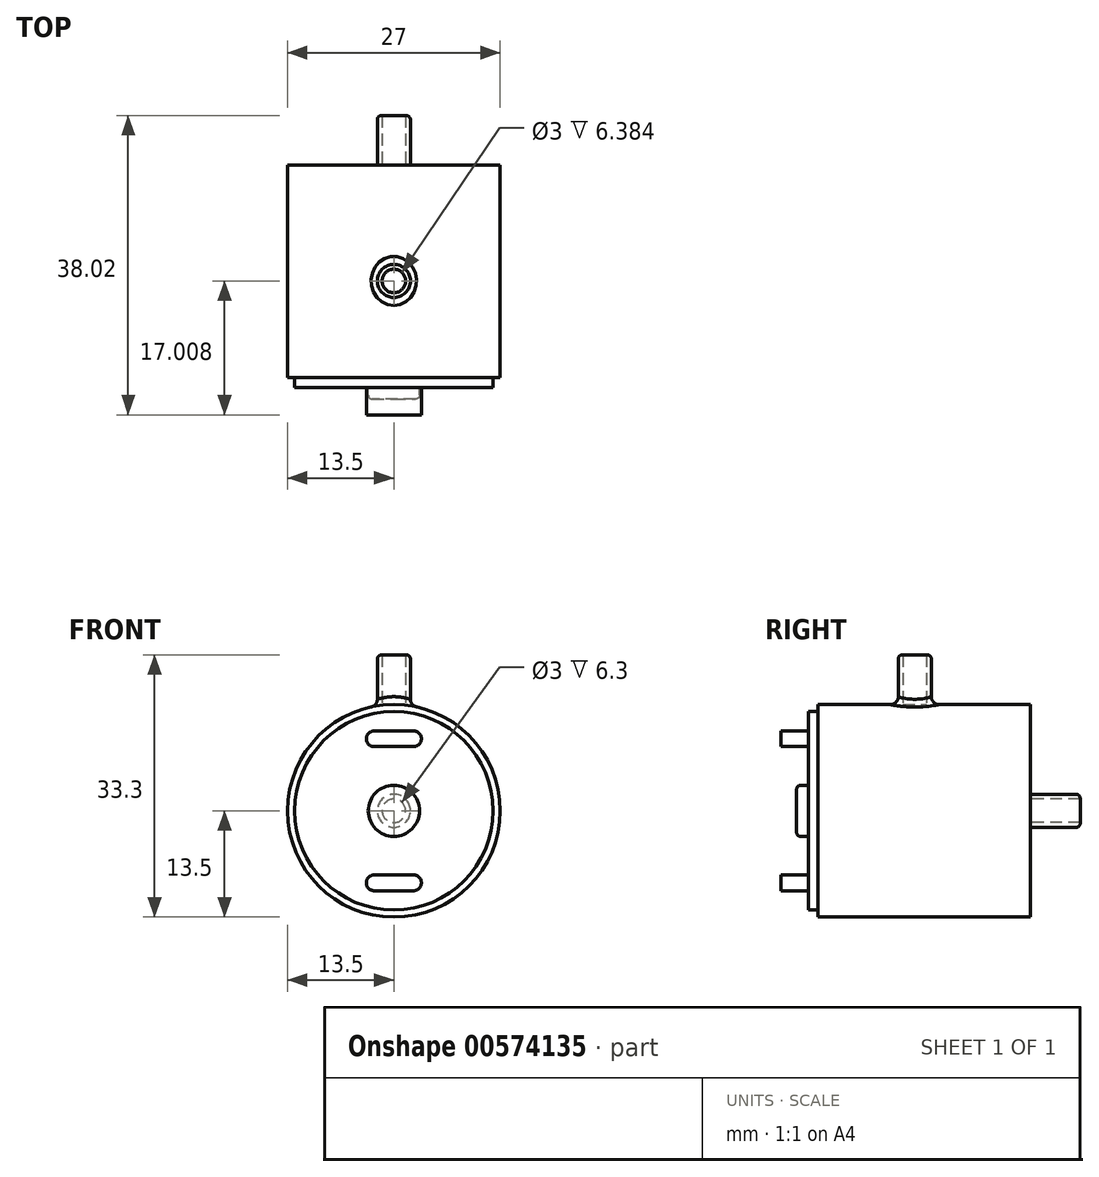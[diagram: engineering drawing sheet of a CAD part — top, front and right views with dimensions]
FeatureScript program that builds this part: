
annotation { "Feature Type Name" : "Feature", "Feature Type Description" : "" }
export const myFeature = defineFeature(function(context is Context, id is Id, definition is map)
    precondition{}
    {
        {
            var Q0;
            Q0=qCreatedBy(makeId("Front.planeOp"),FACE);
            var sketch = newSketch(context, id + "F0", { "sketchPlane" : qUnion([Q0])});
            skCircle(sketch, "E0", {"center": v(0, 0) * mm, "radius": 13.5 * mm});
            skSolve(sketch);
        }
        {
            var Q0;
            Q0 = qSketchRegion(id + "F0", true);
            extrude(context, id + "F1", {"entities" : qUnion([Q0]), "depth" : 27 * mm, "offsetDistance" : 25.4 * mm});
        }
        {
            var Q0;
            Q0=makeQuery(id+"F1.opExtrude","CAP_FACE",FACE,{"disambiguationData":[OSD([sQuery(id+"F0.wireOp",EDGE,"E0")])],"isStart":false});
            var sketch = newSketch(context, id + "F2", { "sketchPlane" : qUnion([Q0])});
            skCircle(sketch, "E1", {"center": v(0, 0) * mm, "radius": 12.6 * mm});
            skSolve(sketch);
        }
        {
            var Q0;
            Q0 = qSketchRegion(id + "F2", true);
            extrude(context, id + "F3", {"entities" : qUnion([Q0]), "operationType" : NewBodyOperationType.ADD, "depth" : ((58 - 27) / 25.4) * mm, "offsetDistance" : 25.4 * mm});
        }
        {
            var Q0;
            Q0=makeQuery(id+"F1.opExtrude","CAP_FACE",FACE,{"disambiguationData":[OSD([sQuery(id+"F0.wireOp",EDGE,"E0")])],"isStart":true});
            var sketch = newSketch(context, id + "F4", { "sketchPlane" : qUnion([Q0])});
            skCircle(sketch, "E2", {"center": v(0, 0) * mm, "radius": 2.1 * mm});
            skCircle(sketch, "E3", {"center": v(0, 0) * mm, "radius": 1.5 * mm});
            skSolve(sketch);
        }
        {
            var Q0;
            Q0 = qSketchRegion(id + "F4", true);
            extrude(context, id + "F5", {"entities" : qUnion([Q0]), "operationType" : NewBodyOperationType.ADD, "depth" : 6.3 * mm, "offsetDistance" : 25.4 * mm});
        }
        {
            var Q0;
            Q0=qCreatedBy(makeId("Top.planeOp"),FACE);
            var sketch = newSketch(context, id + "F6", { "sketchPlane" : qUnion([Q0])});
            skCircle(sketch, "E4", {"center": v(0, -14.71) * mm, "radius": 2.1 * mm});
            skCircle(sketch, "E5", {"center": v(0, -14.71) * mm, "radius": 1.5 * mm});
            skSolve(sketch);
        }
        {
            var Q0;
            Q0 = qSketchRegion(id + "F6", true);
            extrude(context, id + "F7", {"entities" : qUnion([Q0]), "operationType" : NewBodyOperationType.ADD, "depth" : 19.8 * mm, "offsetDistance" : 25.4 * mm});
        }
        {
            var Q0;
            Q0=makeQuery(id+"F5.opExtrude","CAP_EDGE",EDGE,{"disambiguationData":[OSD([sQuery(id+"F4.wireOp",EDGE,"E2")])],"isStart":true});
            var Q1;
            Q1=makeQuery(id+"F7.boolean.opBoolean","INTERSECT",EDGE,{"derivedFrom":[makeQuery(id+"F1.opExtrude","SWEPT_FACE",FACE,{"disambiguationData":[OSD([sQuery(id+"F0.wireOp",EDGE,"E0")])]}),makeQuery(id+"F7.opExtrude","SWEPT_FACE",FACE,{"disambiguationData":[OSD([sQuery(id+"F6.wireOp",EDGE,"E4")])]})]});
            fillet(context, id + "F8", {"entities" : qUnion([Q0, Q1]), "radius" : 1 * mm, "tangentPropagation" : true, "allowEdgeOverflow" : false});
        }
        {
            var Q0;
            Q0=makeQuery(id+"F3.opExtrude","CAP_FACE",FACE,{"disambiguationData":[OSD([sQuery(id+"F2.wireOp",EDGE,"E1")])],"isStart":false});
            var sketch = newSketch(context, id + "F9", { "sketchPlane" : qUnion([Q0])});
            skLineSegment(sketch, "E6", {"start": v(-2.5, 10.15) * mm, "end": v(2.5, 10.15) * mm});
            skLineSegment(sketch, "E7", {"start": v(2.5, 8.15) * mm, "end": v(-2.5, 8.15) * mm});
            skArc(sketch, "E8", {"start": v(-2.5, 10.15) * mm, "mid": v(-3.5, 9.15) * mm, "end": v(-2.5, 8.15) * mm});
            skArc(sketch, "E9", {"start": v(2.5, 8.15) * mm, "mid": v(3.5, 9.15) * mm, "end": v(2.5, 10.15) * mm});
            skPoint(sketch, "E10", {"position": v(0, 10.15) * mm});
            skPoint(sketch, "E11.MirrorP", {"position": v(0, -10.15) * mm});
            skLineSegment(sketch, "E12.MirrorCS", {"start": v(-2.5, -10.15) * mm, "end": v(2.5, -10.15) * mm});
            skLineSegment(sketch, "E13.MirrorCS", {"start": v(2.5, -8.15) * mm, "end": v(-2.5, -8.15) * mm});
            skArc(sketch, "E14.MirrorCS", {"start": v(-2.5, -10.15) * mm, "mid": v(-3.5, -9.15) * mm, "end": v(-2.5, -8.15) * mm});
            skArc(sketch, "E15.MirrorCS", {"start": v(2.5, -8.15) * mm, "mid": v(3.5, -9.15) * mm, "end": v(2.5, -10.15) * mm});
            skSolve(sketch);
        }
        {
            var Q0;
            Q0 = qSketchRegion(id + "F9", true);
            extrude(context, id + "F10", {"entities" : qUnion([Q0]), "operationType" : NewBodyOperationType.ADD, "depth" : 3.5 * mm, "offsetDistance" : 25.4 * mm});
        }
        {
            var Q0;
            Q0=makeQuery(id+"F3.opExtrude","CAP_FACE",FACE,{"disambiguationData":[OSD([sQuery(id+"F2.wireOp",EDGE,"E1")])],"isStart":false});
            var sketch = newSketch(context, id + "F11", { "sketchPlane" : qUnion([Q0])});
            skCircle(sketch, "E16", {"center": v(0, 0) * mm, "radius": 3.25 * mm});
            skSolve(sketch);
        }
        {
            var Q0;
            Q0 = qSketchRegion(id + "F11", true);
            extrude(context, id + "F12", {"entities" : qUnion([Q0]), "operationType" : NewBodyOperationType.ADD, "depth" : 1.5 * mm, "offsetDistance" : 25.4 * mm});
        }
        {
            var Q0;
            Q0=makeQuery(id+"F5.opExtrude","CAP_EDGE",EDGE,{"disambiguationData":[OSD([sQuery(id+"F4.wireOp",EDGE,"E2")])],"isStart":false});
            var Q1;
            Q1=makeQuery(id+"F7.opExtrude","CAP_EDGE",EDGE,{"disambiguationData":[OSD([sQuery(id+"F6.wireOp",EDGE,"E4")])],"isStart":false});
            var Q2;
            Q2=makeQuery(id+"F12.opExtrude","CAP_EDGE",EDGE,{"disambiguationData":[OSD([sQuery(id+"F11.wireOp",EDGE,"E16")])],"isStart":false});
            fillet(context, id + "F13", {"entities" : qUnion([Q0, Q1, Q2]), "radius" : .5 * mm, "tangentPropagation" : true, "allowEdgeOverflow" : false});
        }
    });
